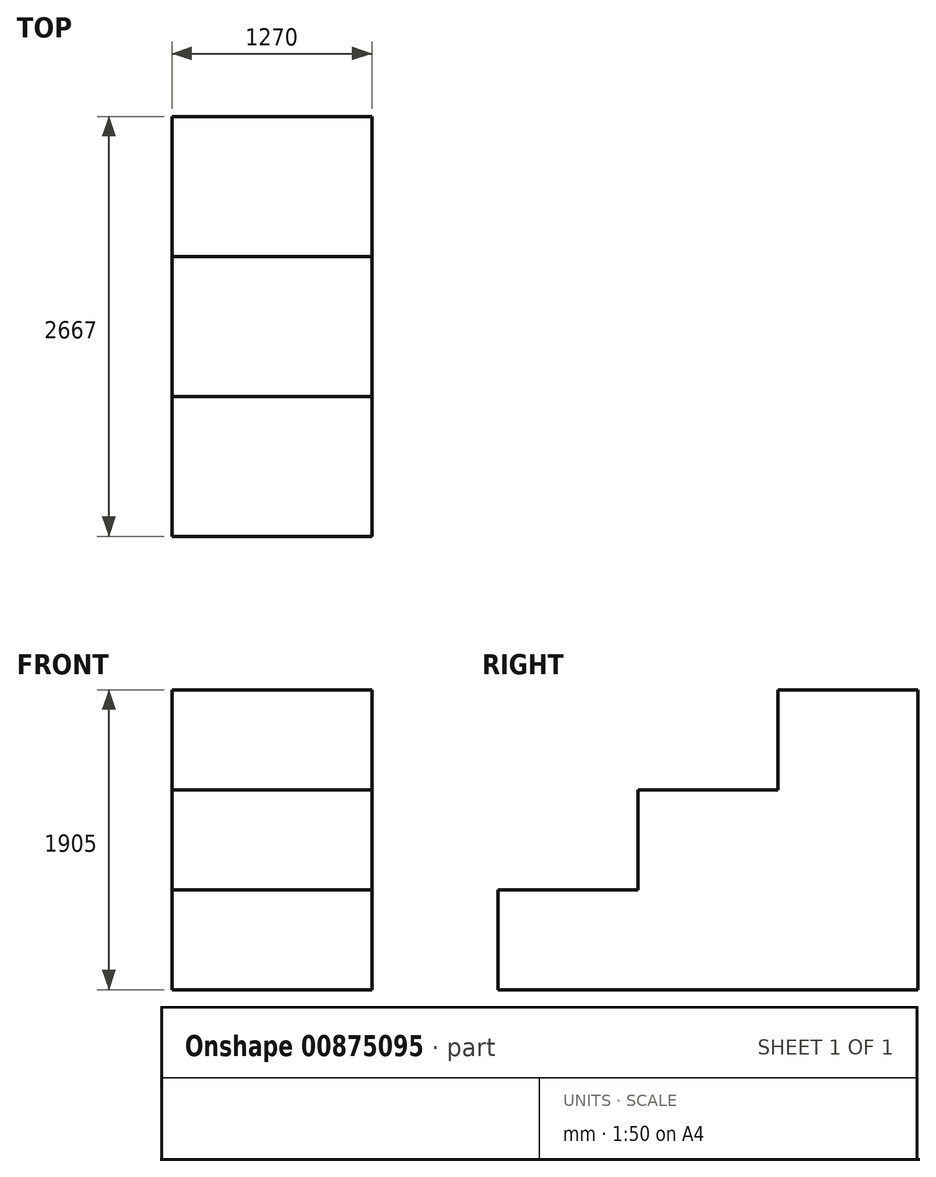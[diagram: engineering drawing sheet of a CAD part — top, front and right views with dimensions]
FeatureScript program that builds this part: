
annotation { "Feature Type Name" : "Feature", "Feature Type Description" : "" }
export const myFeature = defineFeature(function(context is Context, id is Id, definition is map)
    precondition{}
    {
        {
            var Q0;
            Q0=qCreatedBy(makeId("Right.planeOp"),FACE);
            var sketch = newSketch(context, id + "F0", { "sketchPlane" : qUnion([Q0])});
            skLineSegment(sketch, "E0", {"start": v(-28.53, 629.79) * mm, "end": v(-28.53, -5.21) * mm});
            skLineSegment(sketch, "E1", {"start": v(-28.53, -5.21) * mm, "end": v(2638.47, -5.21) * mm});
            skLineSegment(sketch, "E2", {"start": v(2638.47, -5.21) * mm, "end": v(2638.47, 1899.79) * mm});
            skLineSegment(sketch, "E3", {"start": v(2638.47, 1899.79) * mm, "end": v(1749.47, 1899.79) * mm});
            skLineSegment(sketch, "E4", {"start": v(1749.47, 1899.79) * mm, "end": v(1749.47, 1264.79) * mm});
            skLineSegment(sketch, "E5", {"start": v(1749.47, 1264.79) * mm, "end": v(860.47, 1264.79) * mm});
            skLineSegment(sketch, "E6", {"start": v(860.47, 1264.79) * mm, "end": v(860.47, 629.79) * mm});
            skLineSegment(sketch, "E7", {"start": v(860.47, 629.79) * mm, "end": v(-28.53, 629.79) * mm});
            skSolve(sketch);
        }
        {
            var Q0;
            Q0=makeQuery(id+"F0.imprint","IMPRINT",FACE,{"disambiguationData":[TD([[makeQuery(id+"F0.imprint","IMPRINT",EDGE,{"derivedFrom":sQuery(id+"F0.wireOp",EDGE,"E0")}),1.0]])]});
            extrude(context, id + "F1", {"entities" : qUnion([Q0]), "depth" : 1270 * mm, "offsetDistance" : 25.4 * mm});
        }
    });
